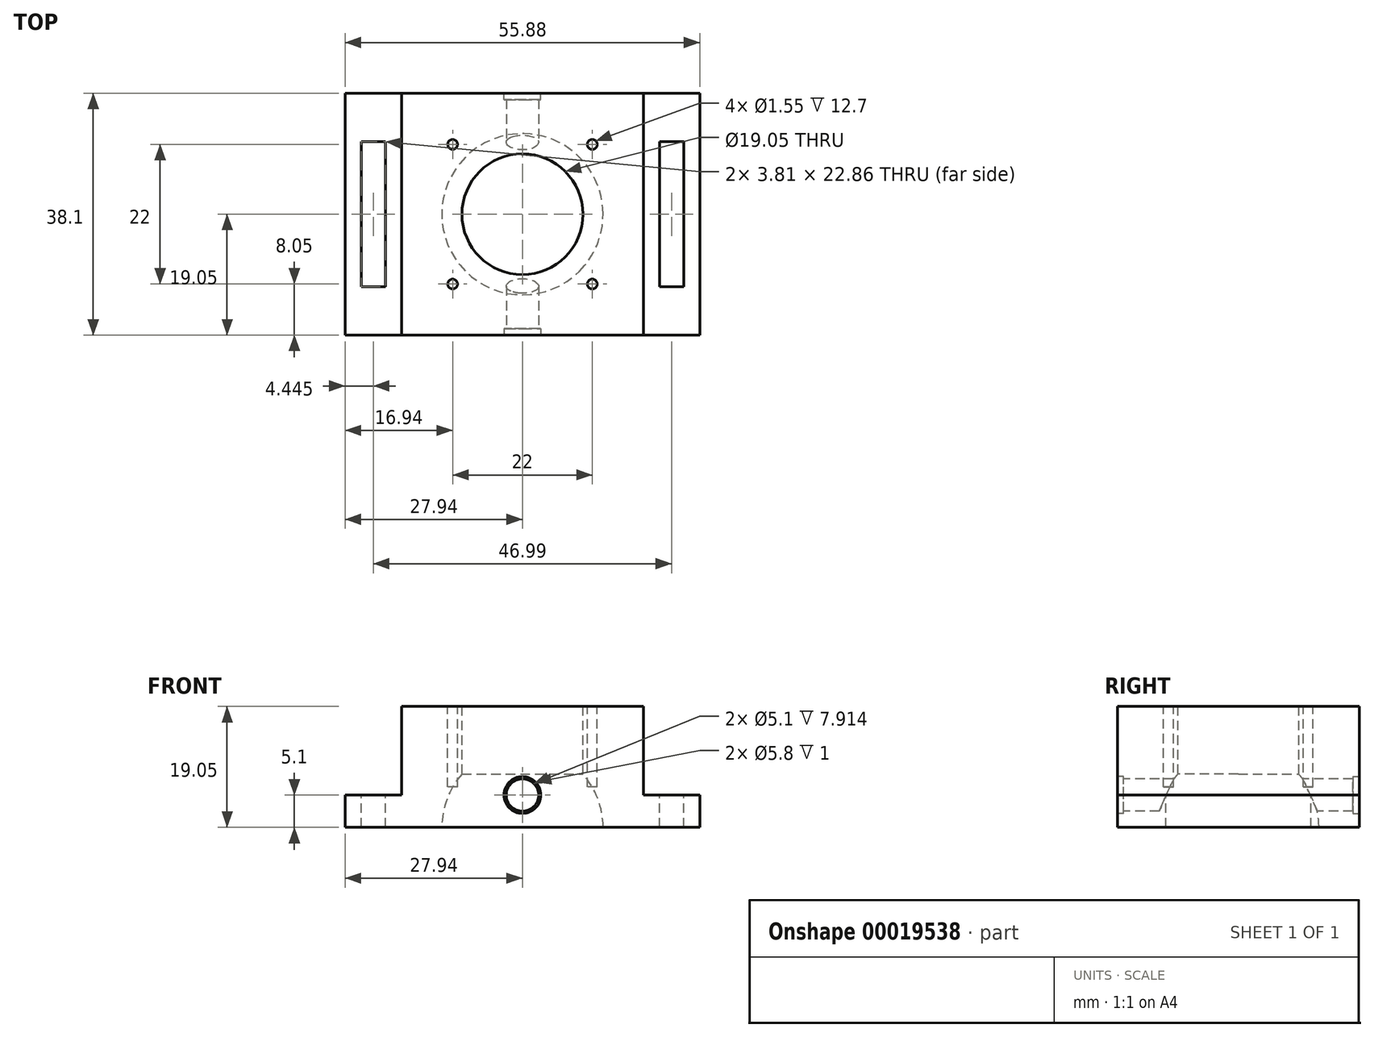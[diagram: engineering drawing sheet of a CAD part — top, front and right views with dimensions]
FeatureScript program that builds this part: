
annotation { "Feature Type Name" : "Feature", "Feature Type Description" : "" }
export const myFeature = defineFeature(function(context is Context, id is Id, definition is map)
    precondition{}
    {
        {
            var Q0;
            Q0=qCreatedBy(makeId("Top.planeOp"),FACE);
            var sketch = newSketch(context, id + "F0", { "sketchPlane" : qUnion([Q0])});
            skLineSegment(sketch, "E0.bottom", {"start": v(0, 0) * mm, "end": v(38.1, 0) * mm});
            skLineSegment(sketch, "E0.top", {"start": v(0, 38.1) * mm, "end": v(38.1, 38.1) * mm});
            skLineSegment(sketch, "E0.left", {"start": v(0, 0) * mm, "end": v(0, 38.1) * mm});
            skLineSegment(sketch, "E0.right", {"start": v(38.1, 0) * mm, "end": v(38.1, 38.1) * mm});
            skSolve(sketch);
        }
        {
            var Q0;
            Q0=makeQuery(id+"F0.imprint","IMPRINT",FACE,{"disambiguationData":[TD([[makeQuery(id+"F0.imprint","IMPRINT",EDGE,{"derivedFrom":sQuery(id+"F0.wireOp",EDGE,"E0.bottom")}),1.0]])]});
            extrude(context, id + "F1", {"entities" : qUnion([Q0]), "depth" : 19.05 * mm});
        }
        {
            var Q0;
            Q0=makeQuery(id+"F1.opExtrude","CAP_FACE",FACE,{"disambiguationData":[OSD([sQuery(id+"F0.wireOp",EDGE,"E0.bottom"),sQuery(id+"F0.wireOp",EDGE,"E0.top"),sQuery(id+"F0.wireOp",EDGE,"E0.left"),sQuery(id+"F0.wireOp",EDGE,"E0.right")])],"isStart":false});
            var sketch = newSketch(context, id + "F2", { "sketchPlane" : qUnion([Q0])});
            skCircle(sketch, "E1", {"center": v(8.05, 30.05) * mm, "radius": 0.77 * mm});
            skCircle(sketch, "E2", {"center": v(8.05, 8.05) * mm, "radius": 0.77 * mm});
            skCircle(sketch, "E3", {"center": v(30.05, 30.05) * mm, "radius": 0.77 * mm});
            skCircle(sketch, "E4", {"center": v(30.05, 8.05) * mm, "radius": 0.77 * mm});
            skLineSegment(sketch, "E5", {"start": v(8.05, 30.05) * mm, "end": v(30.05, 30.05) * mm, "construction": true});
            skLineSegment(sketch, "E6", {"start": v(8.05, 8.05) * mm, "end": v(30.05, 8.05) * mm, "construction": true});
            skLineSegment(sketch, "E7", {"start": v(30.05, 30.05) * mm, "end": v(30.05, 8.05) * mm, "construction": true});
            skLineSegment(sketch, "E8", {"start": v(8.05, 30.05) * mm, "end": v(8.05, 8.05) * mm, "construction": true});
            skLineSegment(sketch, "E9", {"start": v(0, 0) * mm, "end": v(38.1, 38.1) * mm, "construction": true});
            skLineSegment(sketch, "E10", {"start": v(0, 38.1) * mm, "end": v(38.1, 0) * mm, "construction": true});
            skSolve(sketch);
        }
        {
            var Q0;
            Q0 = qSketchRegion(id + "F2", true);
            extrude(context, id + "F3", {"entities" : qUnion([Q0]), "operationType" : NewBodyOperationType.REMOVE, "oppositeDirection" : true, "depth" : 12.7 * mm});
        }
        {
            var Q0;
            Q0=makeQuery(id+"F1.opExtrude","CAP_FACE",FACE,{"disambiguationData":[OSD([sQuery(id+"F0.wireOp",EDGE,"E0.bottom"),sQuery(id+"F0.wireOp",EDGE,"E0.top"),sQuery(id+"F0.wireOp",EDGE,"E0.left"),sQuery(id+"F0.wireOp",EDGE,"E0.right")])],"isStart":false});
            var sketch = newSketch(context, id + "F4", { "sketchPlane" : qUnion([Q0])});
            skLineSegment(sketch, "E11", {"start": v(0, 38.1) * mm, "end": v(38.1, 0) * mm, "construction": true});
            skPoint(sketch, "E12", {"position": v(19.05, 19.05) * mm});
            skCircle(sketch, "E13", {"center": v(19.05, 19.05) * mm, "radius": 9.53 * mm});
            skSolve(sketch);
        }
        {
            var Q0;
            Q0 = qSketchRegion(id + "F4", true);
            extrude(context, id + "F5", {"entities" : qUnion([Q0]), "operationType" : NewBodyOperationType.REMOVE, "endBound" : BoundingType.THROUGH_ALL, "oppositeDirection" : true, "depth" : 25.4 * mm});
        }
        {
            var Q0;
            Q0=makeQuery(id+"F1.opExtrude","CAP_FACE",FACE,{"disambiguationData":[OSD([sQuery(id+"F0.wireOp",EDGE,"E0.bottom"),sQuery(id+"F0.wireOp",EDGE,"E0.top"),sQuery(id+"F0.wireOp",EDGE,"E0.left"),sQuery(id+"F0.wireOp",EDGE,"E0.right")])],"isStart":true});
            var sketch = newSketch(context, id + "F6", { "sketchPlane" : qUnion([Q0])});
            skLineSegment(sketch, "E14", {"start": v(0, -38.1) * mm, "end": v(38.1, 0) * mm, "construction": true});
            skArc(sketch, "E15", {"start": v(10.07, -28.03) * mm, "mid": v(28.03, -28.03) * mm, "end": v(28.03, -10.07) * mm});
            skLineSegment(sketch, "E16", {"start": v(28.03, -10.07) * mm, "end": v(10.07, -28.03) * mm});
            skSolve(sketch);
        }
        {
            var Q0;
            Q0 = qSketchRegion(id + "F6", true);
            var Q1;
            Q1=sQuery(id+"F6.wireOp",EDGE,"E14");
            revolve(context, id + "F7", {"operationType" : NewBodyOperationType.REMOVE, "entities" : qUnion([Q0]), "axis" : qUnion([Q1]), "revolveType" : RevolveType.FULL, "oppositeDirection" : true});
        }
        {
            var Q0;
            Q0=makeQuery(id+"F1.opExtrude","SWEPT_FACE",FACE,{"disambiguationData":[OSD([sQuery(id+"F0.wireOp",EDGE,"E0.bottom")])]});
            var sketch = newSketch(context, id + "F8", { "sketchPlane" : qUnion([Q0])});
            skCircle(sketch, "E17", {"center": v(19.05, 5.1) * mm, "radius": 2.55 * mm});
            skLineSegment(sketch, "E18", {"start": v(0, 5.1) * mm, "end": v(38.1, 5.1) * mm, "construction": true});
            skSolve(sketch);
        }
        {
            var Q0;
            Q0 = qSketchRegion(id + "F8", true);
            extrude(context, id + "F9", {"entities" : qUnion([Q0]), "operationType" : NewBodyOperationType.REMOVE, "endBound" : BoundingType.THROUGH_ALL, "oppositeDirection" : true, "depth" : 25.4 * mm});
        }
        {
            var Q0;
            Q0=makeQuery(id+"F1.opExtrude","SWEPT_FACE",FACE,{"disambiguationData":[OSD([sQuery(id+"F0.wireOp",EDGE,"E0.bottom")])]});
            var sketch = newSketch(context, id + "F10", { "sketchPlane" : qUnion([Q0])});
            skCircle(sketch, "E19", {"center": v(19.05, 5.1) * mm, "radius": 2.9 * mm});
            skSolve(sketch);
        }
        {
            var Q0;
            Q0 = qSketchRegion(id + "F10", true);
            extrude(context, id + "F11", {"entities" : qUnion([Q0]), "operationType" : NewBodyOperationType.REMOVE, "oppositeDirection" : true, "depth" : 1 * mm});
        }
        {
            var Q0;
            Q0=makeQuery(id+"F1.opExtrude","SWEPT_FACE",FACE,{"disambiguationData":[OSD([sQuery(id+"F0.wireOp",EDGE,"E0.top")])]});
            var sketch = newSketch(context, id + "F12", { "sketchPlane" : qUnion([Q0])});
            skCircle(sketch, "E20", {"center": v(-19.05, 5.1) * mm, "radius": 2.9 * mm});
            skSolve(sketch);
        }
        {
            var Q0;
            Q0 = qSketchRegion(id + "F12", true);
            extrude(context, id + "F13", {"entities" : qUnion([Q0]), "operationType" : NewBodyOperationType.REMOVE, "oppositeDirection" : true, "depth" : 1 * mm});
        }
        {
            var Q0;
            Q0=makeQuery(id+"F1.opExtrude","SWEPT_FACE",FACE,{"disambiguationData":[OSD([sQuery(id+"F0.wireOp",EDGE,"E0.left")])]});
            var sketch = newSketch(context, id + "F14", { "sketchPlane" : qUnion([Q0])});
            skLineSegment(sketch, "E21.bottom", {"start": v(-38.1, 0) * mm, "end": v(0, 0) * mm});
            skLineSegment(sketch, "E21.top", {"start": v(-38.1, 5.08) * mm, "end": v(0, 5.08) * mm});
            skLineSegment(sketch, "E21.left", {"start": v(-38.1, 0) * mm, "end": v(-38.1, 5.08) * mm});
            skLineSegment(sketch, "E21.right", {"start": v(0, 0) * mm, "end": v(0, 5.08) * mm});
            skSolve(sketch);
        }
        {
            var Q0;
            Q0 = qSketchRegion(id + "F14", true);
            extrude(context, id + "F15", {"entities" : qUnion([Q0]), "operationType" : NewBodyOperationType.ADD, "depth" : 8.9 * mm});
        }
        {
            var Q0;
            Q0=makeQuery(id+"F15.opExtrude","SWEPT_FACE",FACE,{"disambiguationData":[OSD([sQuery(id+"F14.wireOp",EDGE,"E21.top")])]});
            var sketch = newSketch(context, id + "F16", { "sketchPlane" : qUnion([Q0])});
            skLineSegment(sketch, "E22.bottom", {"start": v(-6.35, 30.48) * mm, "end": v(-2.54, 30.48) * mm});
            skLineSegment(sketch, "E22.top", {"start": v(-6.35, 7.62) * mm, "end": v(-2.54, 7.62) * mm});
            skLineSegment(sketch, "E22.left", {"start": v(-6.35, 30.48) * mm, "end": v(-6.35, 7.62) * mm});
            skLineSegment(sketch, "E22.right", {"start": v(-2.54, 30.48) * mm, "end": v(-2.54, 7.62) * mm});
            skSolve(sketch);
        }
        {
            var Q0;
            Q0 = qSketchRegion(id + "F16", true);
            extrude(context, id + "F17", {"entities" : qUnion([Q0]), "operationType" : NewBodyOperationType.REMOVE, "oppositeDirection" : true, "depth" : 25.4 * mm});
        }
        {
            var Q0;
            Q0=makeQuery(id+"F1.opExtrude","SWEPT_FACE",FACE,{"disambiguationData":[OSD([sQuery(id+"F0.wireOp",EDGE,"E0.right")])]});
            var sketch = newSketch(context, id + "F18", { "sketchPlane" : qUnion([Q0])});
            skLineSegment(sketch, "E23.bottom", {"start": v(0, 0) * mm, "end": v(38.1, 0) * mm});
            skLineSegment(sketch, "E23.top", {"start": v(0, 5.08) * mm, "end": v(38.1, 5.08) * mm});
            skLineSegment(sketch, "E23.left", {"start": v(0, 0) * mm, "end": v(0, 5.08) * mm});
            skLineSegment(sketch, "E23.right", {"start": v(38.1, 0) * mm, "end": v(38.1, 5.08) * mm});
            skSolve(sketch);
        }
        {
            var Q0;
            Q0 = qSketchRegion(id + "F18", true);
            extrude(context, id + "F19", {"entities" : qUnion([Q0]), "operationType" : NewBodyOperationType.ADD, "depth" : 8.9 * mm});
        }
        {
            var Q0;
            Q0=makeQuery(id+"F19.opExtrude","SWEPT_FACE",FACE,{"disambiguationData":[OSD([sQuery(id+"F18.wireOp",EDGE,"E23.top")])]});
            var sketch = newSketch(context, id + "F20", { "sketchPlane" : qUnion([Q0])});
            skLineSegment(sketch, "E24.bottom", {"start": v(44.45, 7.62) * mm, "end": v(40.64, 7.62) * mm});
            skLineSegment(sketch, "E24.top", {"start": v(44.45, 30.48) * mm, "end": v(40.64, 30.48) * mm});
            skLineSegment(sketch, "E24.left", {"start": v(44.45, 7.62) * mm, "end": v(44.45, 30.48) * mm});
            skLineSegment(sketch, "E24.right", {"start": v(40.64, 7.62) * mm, "end": v(40.64, 30.48) * mm});
            skSolve(sketch);
        }
        {
            var Q0;
            Q0 = qSketchRegion(id + "F20", true);
            extrude(context, id + "F21", {"entities" : qUnion([Q0]), "operationType" : NewBodyOperationType.REMOVE, "oppositeDirection" : true, "depth" : 25.4 * mm});
        }
    });
